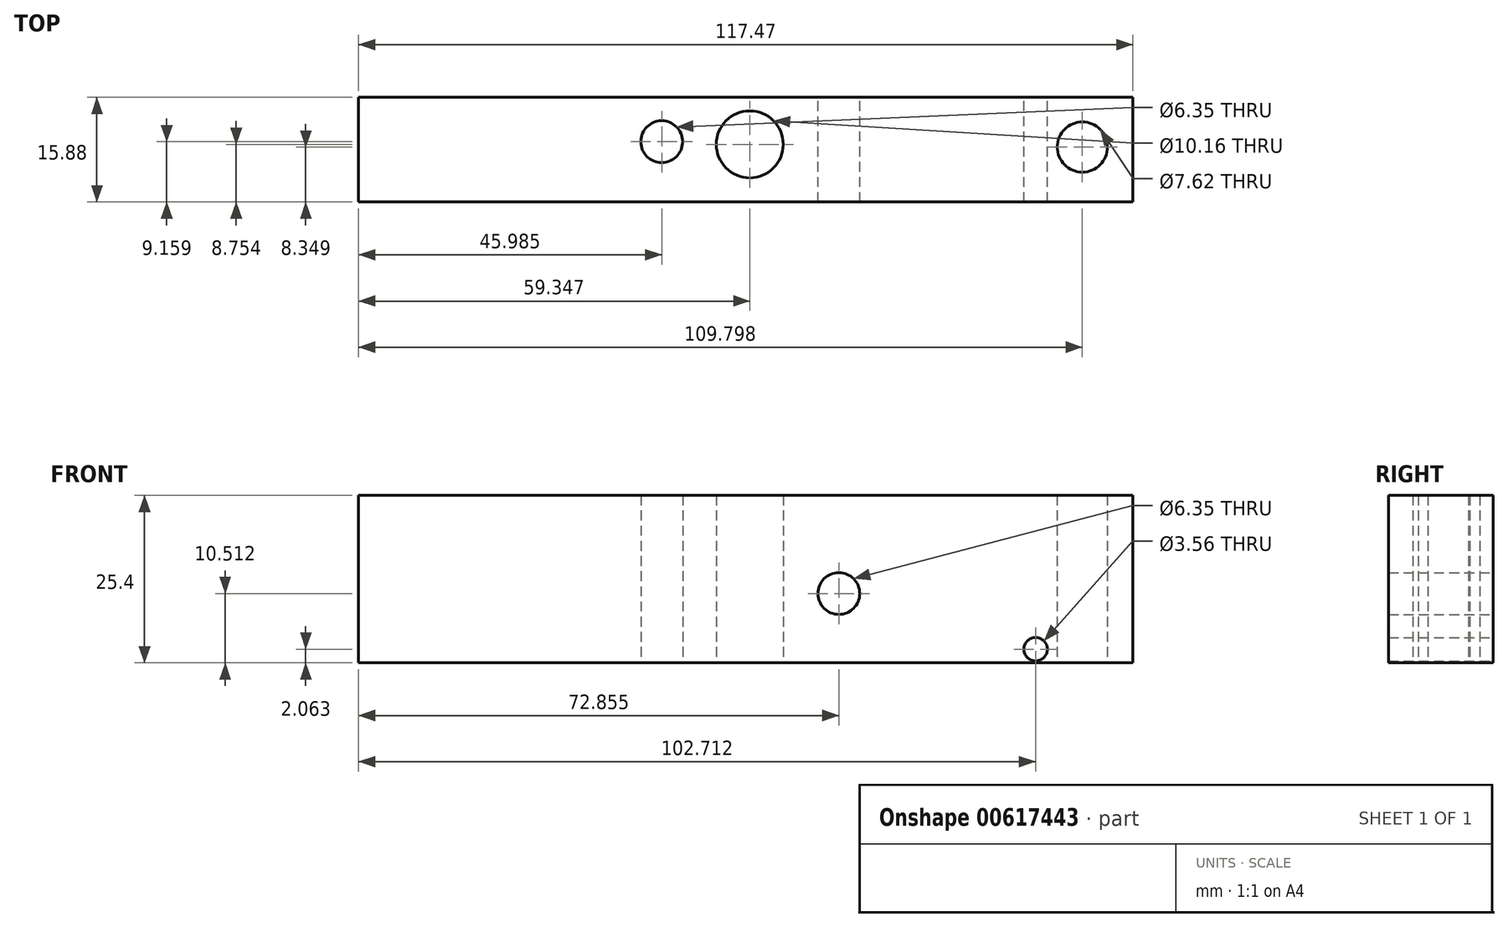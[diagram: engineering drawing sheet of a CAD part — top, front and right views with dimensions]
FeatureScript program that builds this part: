
annotation { "Feature Type Name" : "Feature", "Feature Type Description" : "" }
export const myFeature = defineFeature(function(context is Context, id is Id, definition is map)
    precondition{}
    {
        {
            var Q0;
            Q0=qCreatedBy(makeId("Front.planeOp"),FACE);
            var sketch = newSketch(context, id + "F0", { "sketchPlane" : qUnion([Q0])});
            skLineSegment(sketch, "E0", {"start": v(0, 0) * mm, "end": v(117.48, 0) * mm});
            skLineSegment(sketch, "E1", {"start": v(117.48, 0) * mm, "end": v(117.48, 25.4) * mm});
            skLineSegment(sketch, "E2", {"start": v(117.48, 25.4) * mm, "end": v(0, 25.4) * mm});
            skLineSegment(sketch, "E3", {"start": v(0, 25.4) * mm, "end": v(0, 0) * mm});
            skSolve(sketch);
        }
        {
            var Q0;
            Q0=makeQuery(id+"F0.imprint","IMPRINT",FACE,{"disambiguationData":[TD([[makeQuery(id+"F0.imprint","IMPRINT",EDGE,{"derivedFrom":sQuery(id+"F0.wireOp",EDGE,"E0")}),1.0]])]});
            extrude(context, id + "F1", {"entities" : qUnion([Q0]), "depth" : 15.88 * mm, "offsetDistance" : 25.4 * mm});
        }
        {
            var Q0;
            Q0=qCreatedBy(makeId("Top.planeOp"),FACE);
            var sketch = newSketch(context, id + "F2", { "sketchPlane" : qUnion([Q0])});
            skPoint(sketch, "E4", {"position": v(45.98, -6.72) * mm});
            skSolve(sketch);
        }
        {
            var Q0;
            Q0=sQuery(id+"F2.wireOp",VERTEX,"E4");
            var Q1;
            Q1=makeQuery(id+"F1.opExtrude","SWEPT_BODY",BODY,{"disambiguationData":[OSD([sQuery(id+"F0.wireOp",EDGE,"E0"),sQuery(id+"F0.wireOp",EDGE,"E1"),sQuery(id+"F0.wireOp",EDGE,"E2"),sQuery(id+"F0.wireOp",EDGE,"E3")])]});
            hole(context, id + "F3", {"style" : HoleStyle.SIMPLE, "endStyle" : HoleEndStyle.BLIND, "oppositeDirection" : true, "holeDiameter" : 6.35 * mm, "majorDiameter" : 6.35 * mm, "holeDepth" : 177.8 * mm, "isTappedThrough" : true, "tappedDepth" : 12.7 * mm, "tapClearance" : 3, "locations" : qUnion([Q0]), "scope" : qUnion([Q1])});
        }
        {
            var Q0;
            Q0=qCreatedBy(makeId("Top.planeOp"),FACE);
            var sketch = newSketch(context, id + "F4", { "sketchPlane" : qUnion([Q0])});
            skLineSegment(sketch, "E5", {"start": v(59.35, -15.71) * mm, "end": v(59.35, -8.75) * mm, "construction": true});
            skPoint(sketch, "E6", {"position": v(59.35, -7.13) * mm});
            skSolve(sketch);
        }
        {
            var Q0;
            Q0=sQuery(id+"F4.wireOp",VERTEX,"92f50393-0951-43c4-ad5f-7c90322ba7fc");
            var Q1;
            Q1=sQuery(id+"F4.wireOp",VERTEX,"dda28d0a-661c-4360-9d37-fde7ed04a7ab");
            var Q2;
            Q2=sQuery(id+"F4.wireOp",VERTEX,"e3e18568-2e69-49c5-91dd-451fbf5c3fa3");
            var Q3;
            Q3=sQuery(id+"F4.wireOp",VERTEX,"E6");
            var Q4;
            Q4=makeQuery(id+"F1.opExtrude","SWEPT_BODY",BODY,{"disambiguationData":[OSD([sQuery(id+"F0.wireOp",EDGE,"E0"),sQuery(id+"F0.wireOp",EDGE,"E1"),sQuery(id+"F0.wireOp",EDGE,"E2"),sQuery(id+"F0.wireOp",EDGE,"E3")])]});
            hole(context, id + "F5", {"style" : HoleStyle.SIMPLE, "endStyle" : HoleEndStyle.BLIND, "oppositeDirection" : true, "holeDiameter" : 10.16 * mm, "majorDiameter" : 6.35 * mm, "holeDepth" : 177.8 * mm, "isTappedThrough" : true, "tappedDepth" : 12.7 * mm, "tapClearance" : 3, "locations" : qUnion([Q0, Q1, Q2, Q3]), "scope" : qUnion([Q4])});
        }
        {
            var Q0;
            Q0=qCreatedBy(makeId("Top.planeOp"),FACE);
            var sketch = newSketch(context, id + "F6", { "sketchPlane" : qUnion([Q0])});
            skPoint(sketch, "E7", {"position": v(109.8, -7.53) * mm});
            skSolve(sketch);
        }
        {
            var Q0;
            Q0=sQuery(id+"F6.wireOp",VERTEX,"E7");
            var Q1;
            Q1=makeQuery(id+"F1.opExtrude","SWEPT_BODY",BODY,{"disambiguationData":[OSD([sQuery(id+"F0.wireOp",EDGE,"E0"),sQuery(id+"F0.wireOp",EDGE,"E1"),sQuery(id+"F0.wireOp",EDGE,"E2"),sQuery(id+"F0.wireOp",EDGE,"E3")])]});
            hole(context, id + "F7", {"style" : HoleStyle.SIMPLE, "endStyle" : HoleEndStyle.BLIND, "oppositeDirection" : true, "holeDiameter" : 7.62 * mm, "majorDiameter" : 6.35 * mm, "holeDepth" : 177.8 * mm, "isTappedThrough" : true, "tappedDepth" : 12.7 * mm, "tapClearance" : 3, "locations" : qUnion([Q0]), "scope" : qUnion([Q1])});
        }
        {
            var Q0;
            Q0=qCreatedBy(makeId("Front.planeOp"),FACE);
            var sketch = newSketch(context, id + "F8", { "sketchPlane" : qUnion([Q0])});
            skPoint(sketch, "E8", {"position": v(72.85, 10.51) * mm});
            skSolve(sketch);
        }
        {
            var Q0;
            Q0=sQuery(id+"F8.wireOp",VERTEX,"E8");
            var Q1;
            Q1=makeQuery(id+"F1.opExtrude","SWEPT_BODY",BODY,{"disambiguationData":[OSD([sQuery(id+"F0.wireOp",EDGE,"E0"),sQuery(id+"F0.wireOp",EDGE,"E1"),sQuery(id+"F0.wireOp",EDGE,"E2"),sQuery(id+"F0.wireOp",EDGE,"E3")])]});
            hole(context, id + "F9", {"style" : HoleStyle.SIMPLE, "endStyle" : HoleEndStyle.BLIND, "oppositeDirection" : true, "holeDiameter" : 6.35 * mm, "majorDiameter" : 6.35 * mm, "holeDepth" : 177.8 * mm, "isTappedThrough" : true, "tappedDepth" : 12.7 * mm, "tapClearance" : 3, "locations" : qUnion([Q0]), "scope" : qUnion([Q1])});
        }
        {
            var Q0;
            Q0=qCreatedBy(makeId("Front.planeOp"),FACE);
            var sketch = newSketch(context, id + "F10", { "sketchPlane" : qUnion([Q0])});
            skPoint(sketch, "E9", {"position": v(102.71, 2.06) * mm});
            skSolve(sketch);
        }
        {
            var Q0;
            Q0=sQuery(id+"F10.wireOp",VERTEX,"E9");
            var Q1;
            Q1=makeQuery(id+"F1.opExtrude","SWEPT_BODY",BODY,{"disambiguationData":[OSD([sQuery(id+"F0.wireOp",EDGE,"E0"),sQuery(id+"F0.wireOp",EDGE,"E1"),sQuery(id+"F0.wireOp",EDGE,"E2"),sQuery(id+"F0.wireOp",EDGE,"E3")])]});
            hole(context, id + "F11", {"style" : HoleStyle.SIMPLE, "endStyle" : HoleEndStyle.BLIND, "oppositeDirection" : true, "holeDiameter" : 3.56 * mm, "majorDiameter" : 6.35 * mm, "holeDepth" : 25.4 * mm, "isTappedThrough" : true, "tappedDepth" : 12.7 * mm, "tapClearance" : 3, "locations" : qUnion([Q0]), "scope" : qUnion([Q1])});
        }
    });
